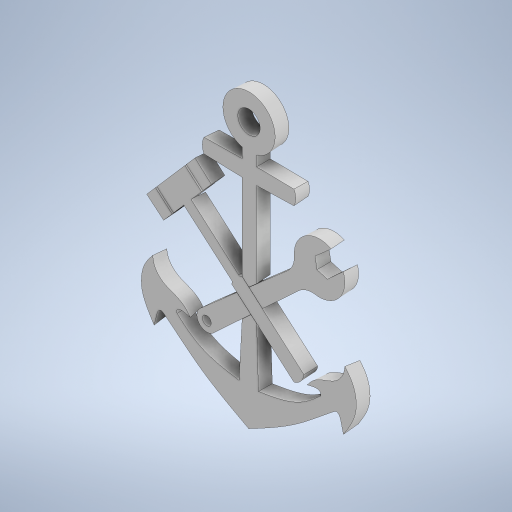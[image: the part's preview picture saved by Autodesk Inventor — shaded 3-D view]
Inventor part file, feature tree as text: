
AUTODESK INVENTOR PART (.ipt)
format: ipt  version: 2024 (Build 280153000, 153)  size: 508,416 bytes
history: native  units: in
note: dims shown in document units (in); Inventor stores cm internally (conversion verified against a paired STEP export)
features: extrude x1, draft x1, sketch x1
ambient origin geometry x8: Origin, YZ Plane, XZ Plane, XY Plane, X Axis, Y Axis, Z Axis, Center Point
bodies: Body1 (feature_tree)
feature tree (3):
  extrude  "Extrusion3"  Depth=0.125in
  draft  "FaceDraft1"
  sketch  "Sketch4"  dims[d4=0.125in d5=0.0in d6=0.0206in]
